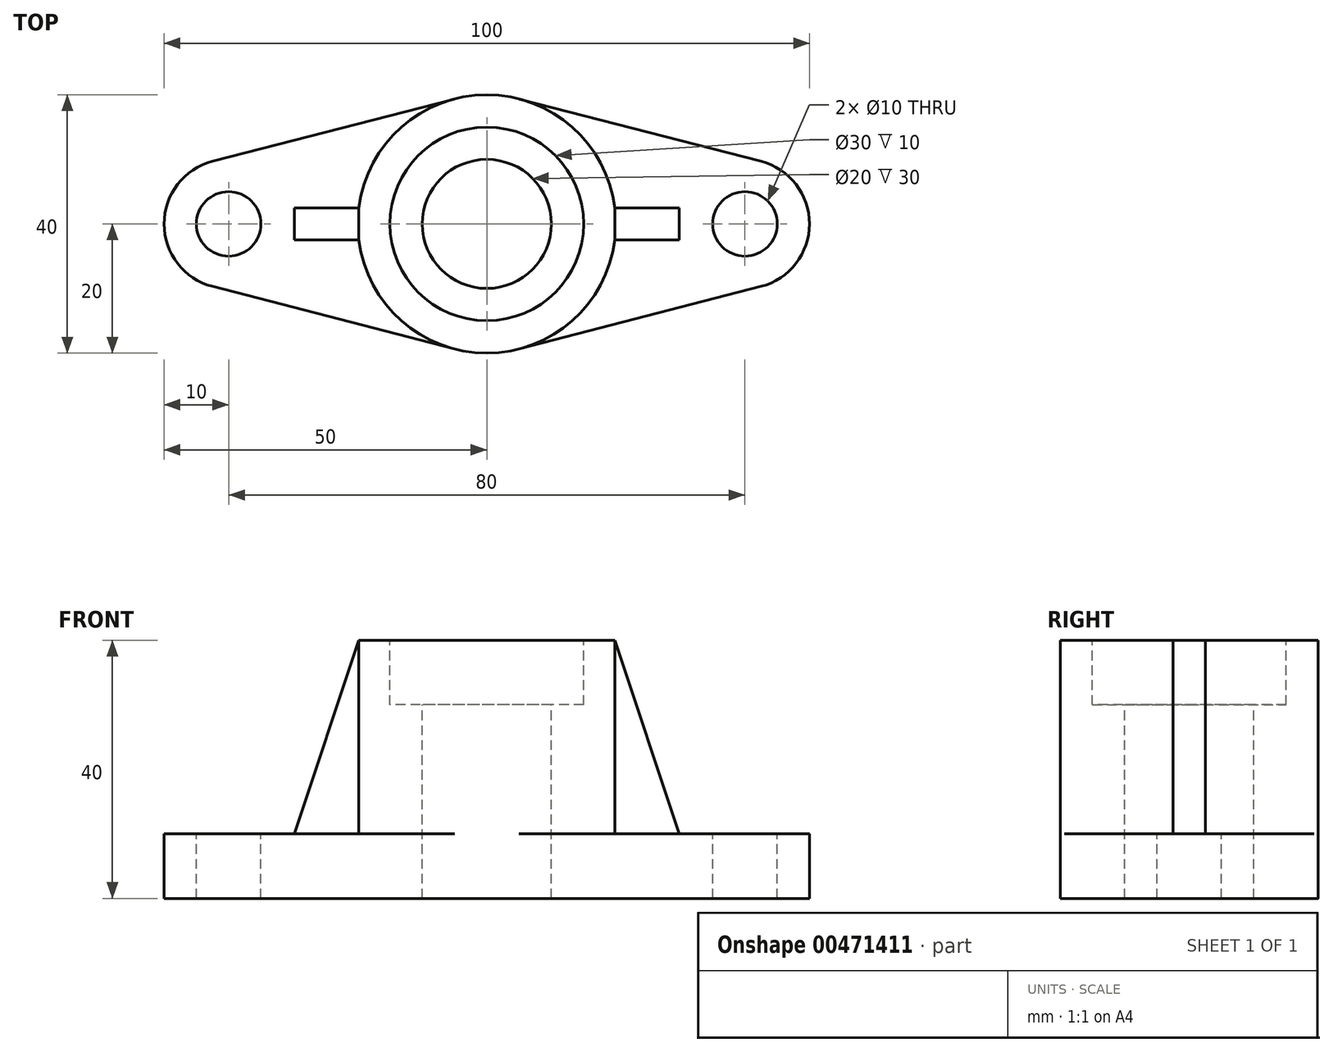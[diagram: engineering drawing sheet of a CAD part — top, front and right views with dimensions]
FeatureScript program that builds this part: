
annotation { "Feature Type Name" : "Feature", "Feature Type Description" : "" }
export const myFeature = defineFeature(function(context is Context, id is Id, definition is map)
    precondition{}
    {
        {
            var Q0;
            Q0=qCreatedBy(makeId("Top.planeOp"),FACE);
            var sketch = newSketch(context, id + "F0", { "sketchPlane" : qUnion([Q0])});
            skArc(sketch, "E0", {"start": v(-5, -19.36) * mm, "mid": v(0, -20) * mm, "end": v(5, -19.36) * mm});
            skLineSegment(sketch, "E1", {"start": v(0, 0) * mm, "end": v(-40, 0) * mm, "construction": true});
            skArc(sketch, "E2", {"start": v(-42.5, 9.68) * mm, "mid": v(-50, 0) * mm, "end": v(-42.5, -9.68) * mm});
            skLineSegment(sketch, "E3", {"start": v(0, 26.92) * mm, "end": v(0, -30.96) * mm, "construction": true});
            skArc(sketch, "E4.MirrorC", {"start": v(42.5, 9.68) * mm, "mid": v(50, 0) * mm, "end": v(42.5, -9.68) * mm});
            skLineSegment(sketch, "E5", {"start": v(42.5, -9.68) * mm, "end": v(5, -19.36) * mm});
            skLineSegment(sketch, "E6", {"start": v(42.5, 9.68) * mm, "end": v(5, 19.36) * mm});
            skLineSegment(sketch, "E7.MirrorCS", {"start": v(-42.5, 9.68) * mm, "end": v(-5, 19.36) * mm});
            skLineSegment(sketch, "E8.MirrorCS", {"start": v(-42.5, -9.68) * mm, "end": v(-5, -19.36) * mm});
            skArc(sketch, "E9.trimOffspring", {"start": v(5.13, 19.33) * mm, "mid": v(0, 20) * mm, "end": v(-5.13, 19.33) * mm});
            skSolve(sketch);
        }
        {
            var Q0;
            Q0 = qSketchRegion(id + "F0", true);
            extrude(context, id + "F1", {"entities" : qUnion([Q0]), "depth" : 10 * mm});
        }
        {
            var Q0;
            Q0=makeQuery(id+"F1.opExtrude","CAP_FACE",FACE,{"disambiguationData":[OSD([sQuery(id+"F0.wireOp",EDGE,"E0"),sQuery(id+"F0.wireOp",EDGE,"E2"),sQuery(id+"F0.wireOp",EDGE,"E4.MirrorC"),sQuery(id+"F0.wireOp",EDGE,"E5"),sQuery(id+"F0.wireOp",EDGE,"E6"),sQuery(id+"F0.wireOp",EDGE,"E7.MirrorCS"),sQuery(id+"F0.wireOp",EDGE,"E8.MirrorCS"),sQuery(id+"F0.wireOp",EDGE,"E9.trimOffspring")])],"isStart":false});
            var sketch = newSketch(context, id + "F2", { "sketchPlane" : qUnion([Q0])});
            skCircle(sketch, "E10", {"center": v(-40, 0) * mm, "radius": 5 * mm});
            skLineSegment(sketch, "E11", {"start": v(0, 27.65) * mm, "end": v(0, -27.09) * mm, "construction": true});
            skPoint(sketch, "E11.startSnap0", {"position": v(0, 20) * mm});
            skPoint(sketch, "E11.endSnap0", {"position": v(0, -20) * mm});
            skCircle(sketch, "E12.MirrorC", {"center": v(40, 0) * mm, "radius": 5 * mm});
            skSolve(sketch);
        }
        {
            var Q0;
            Q0 = qSketchRegion(id + "F2", true);
            extrude(context, id + "F3", {"entities" : qUnion([Q0]), "operationType" : NewBodyOperationType.REMOVE, "endBound" : BoundingType.THROUGH_ALL, "oppositeDirection" : true, "depth" : 25 * mm});
        }
        {
            var Q0;
            Q0=makeQuery(id+"F1.opExtrude","CAP_FACE",FACE,{"disambiguationData":[OSD([sQuery(id+"F0.wireOp",EDGE,"E0"),sQuery(id+"F0.wireOp",EDGE,"E2"),sQuery(id+"F0.wireOp",EDGE,"E4.MirrorC"),sQuery(id+"F0.wireOp",EDGE,"E5"),sQuery(id+"F0.wireOp",EDGE,"E6"),sQuery(id+"F0.wireOp",EDGE,"E7.MirrorCS"),sQuery(id+"F0.wireOp",EDGE,"E8.MirrorCS"),sQuery(id+"F0.wireOp",EDGE,"E9.trimOffspring")])],"isStart":false});
            var sketch = newSketch(context, id + "F4", { "sketchPlane" : qUnion([Q0])});
            skCircle(sketch, "E13", {"center": v(0, 0) * mm, "radius": 20 * mm});
            skSolve(sketch);
        }
        {
            var Q0;
            Q0 = qSketchRegion(id + "F4", true);
            extrude(context, id + "F5", {"entities" : qUnion([Q0]), "operationType" : NewBodyOperationType.ADD, "depth" : 30 * mm});
        }
        {
            var Q0;
            Q0=makeQuery(id+"F5.opExtrude","CAP_FACE",FACE,{"disambiguationData":[OSD([sQuery(id+"F4.wireOp",EDGE,"E13")])],"isStart":false});
            var sketch = newSketch(context, id + "F6", { "sketchPlane" : qUnion([Q0])});
            skCircle(sketch, "E14", {"center": v(0, 0) * mm, "radius": 15 * mm});
            skSolve(sketch);
        }
        {
            var Q0;
            Q0 = qSketchRegion(id + "F6", true);
            extrude(context, id + "F7", {"entities" : qUnion([Q0]), "operationType" : NewBodyOperationType.REMOVE, "oppositeDirection" : true, "depth" : 10 * mm});
        }
        {
            var Q0;
            Q0=makeQuery(id+"F7.boolean.opBoolean","COPY",FACE,{"derivedFrom":makeQuery(id+"F7.opExtrude","CAP_FACE",FACE,{"disambiguationData":[OSD([sQuery(id+"F6.wireOp",EDGE,"E14")])],"isStart":false})});
            var sketch = newSketch(context, id + "F8", { "sketchPlane" : qUnion([Q0])});
            skCircle(sketch, "E15", {"center": v(0, 0) * mm, "radius": 10 * mm});
            skSolve(sketch);
        }
        {
            var Q0;
            Q0 = qSketchRegion(id + "F8", true);
            extrude(context, id + "F9", {"entities" : qUnion([Q0]), "operationType" : NewBodyOperationType.REMOVE, "endBound" : BoundingType.THROUGH_ALL, "oppositeDirection" : true, "depth" : 25 * mm});
        }
        {
            var Q0;
            {var subQ0=sQuery(id+"F0.wireOp",EDGE,"E7.MirrorCS");var subQ1=sQuery(id+"F0.wireOp",EDGE,"E8.MirrorCS");var subQ2=sQuery(id+"F0.wireOp",EDGE,"E2");var subQ3=sQuery(id+"F0.wireOp",EDGE,"E0");var subQ4=sQuery(id+"F0.wireOp",EDGE,"E9.trimOffspring");Q0=makeQuery(id+"F5.boolean.opBoolean","SPLIT",FACE,{"disambiguationData":[TD([makeQuery(id+"F1.opExtrude","SWEPT_FACE",FACE,{"disambiguationData":[OSD([subQ2])]})])],"derivedFrom":makeQuery(id+"F1.opExtrude","CAP_FACE",FACE,{"disambiguationData":[OSD([subQ3,subQ2,sQuery(id+"F0.wireOp",EDGE,"E4.MirrorC"),sQuery(id+"F0.wireOp",EDGE,"E5"),sQuery(id+"F0.wireOp",EDGE,"E6"),subQ0,subQ1,subQ4])],"isStart":false})});}
            cPlane(context, id + "F10", {"entities" : qUnion([Q0]), "cplaneType" : CPlaneType.OFFSET, "offset" : 0 * mm, "width" : 150 * mm, "height" : 150 * mm});
        }
        {
            var Q0;
            Q0=qCreatedBy(id+"F10.planeOp",FACE);
            var sketch = newSketch(context, id + "F11", { "sketchPlane" : qUnion([Q0])});
            skLineSegment(sketch, "E16", {"start": v(0, 0) * mm, "end": v(-39.65, 0) * mm, "construction": true});
            skLineSegment(sketch, "E17", {"start": v(-19.82, 0) * mm, "end": v(-19.82, -2.5) * mm});
            skLineSegment(sketch, "E18", {"start": v(-19.82, -2.5) * mm, "end": v(-29.82, -2.5) * mm});
            skLineSegment(sketch, "E19", {"start": v(-29.82, -2.5) * mm, "end": v(-29.82, 0) * mm});
            skLineSegment(sketch, "E20.MirrorCS", {"start": v(-19.82, 0) * mm, "end": v(-19.82, 2.5) * mm});
            skLineSegment(sketch, "E21.MirrorCS", {"start": v(-19.82, 2.5) * mm, "end": v(-29.82, 2.5) * mm});
            skLineSegment(sketch, "E22.MirrorCS", {"start": v(-29.82, 2.5) * mm, "end": v(-29.82, 0) * mm});
            skLineSegment(sketch, "E23", {"start": v(0, 21.37) * mm, "end": v(0, -26.12) * mm, "construction": true});
            skLineSegment(sketch, "E24.MirrorCS", {"start": v(19.82, 2.5) * mm, "end": v(29.82, 2.5) * mm});
            skLineSegment(sketch, "E25.MirrorCS", {"start": v(29.82, 2.5) * mm, "end": v(29.82, 0) * mm});
            skLineSegment(sketch, "E26.MirrorCS", {"start": v(19.82, 0) * mm, "end": v(19.82, 2.5) * mm});
            skLineSegment(sketch, "E27.MirrorCS", {"start": v(19.82, 0) * mm, "end": v(19.82, -2.5) * mm});
            skLineSegment(sketch, "E28.MirrorCS", {"start": v(19.82, -2.5) * mm, "end": v(29.82, -2.5) * mm});
            skLineSegment(sketch, "E29.MirrorCS", {"start": v(29.82, -2.5) * mm, "end": v(29.82, 0) * mm});
            skSolve(sketch);
        }
        {
            var Q0;
            Q0 = qSketchRegion(id + "F11", true);
            extrude(context, id + "F12", {"entities" : qUnion([Q0]), "operationType" : NewBodyOperationType.ADD, "depth" : 30 * mm});
        }
        {
            var Q0;
            Q0=makeQuery(id+"F12.opExtrude","SWEPT_FACE",FACE,{"disambiguationData":[OSD([sQuery(id+"F11.wireOp",EDGE,"E18")])]});
            var sketch = newSketch(context, id + "F13", { "sketchPlane" : qUnion([Q0])});
            skLineSegment(sketch, "E30", {"start": v(-29.82, 10) * mm, "end": v(-29.82, 40) * mm});
            skLineSegment(sketch, "E31", {"start": v(-29.82, 10) * mm, "end": v(-19.84, 40) * mm});
            skLineSegment(sketch, "E32", {"start": v(-19.84, 40) * mm, "end": v(-29.82, 40) * mm});
            skLineSegment(sketch, "E33", {"start": v(0, 0) * mm, "end": v(0, 43.15) * mm, "construction": true});
            skLineSegment(sketch, "E34.MirrorCS", {"start": v(29.82, 10) * mm, "end": v(19.84, 40) * mm});
            skLineSegment(sketch, "E35.MirrorCS", {"start": v(29.82, 10) * mm, "end": v(29.82, 40) * mm});
            skLineSegment(sketch, "E36.MirrorCS", {"start": v(19.84, 40) * mm, "end": v(29.82, 40) * mm});
            skSolve(sketch);
        }
        {
            var Q0;
            Q0 = qSketchRegion(id + "F13", true);
            extrude(context, id + "F14", {"entities" : qUnion([Q0]), "operationType" : NewBodyOperationType.REMOVE, "endBound" : BoundingType.THROUGH_ALL, "oppositeDirection" : true, "depth" : 25 * mm});
        }
    });
